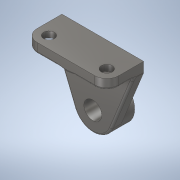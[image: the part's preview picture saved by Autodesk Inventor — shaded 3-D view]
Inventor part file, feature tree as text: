
AUTODESK INVENTOR PART (.ipt)
format: ipt  version: 2020 (Build 240168000, 168)  size: 650,240 bytes
history: native  units: mm
features: extrude x5, sketch x4, fillet x2, plane x1, rib x1
ambient origin geometry x8: Origin, YZ Plane, XZ Plane, XY Plane, X Axis, Y Axis, Z Axis, Center Point
bodies: Solid1 (feature_tree)
feature tree (13):
  extrude  "Extrusion1"  Depth=41.0mm
  sketch  "Sketch2"  dims[d2=18.0mm d3=22.0mm d4=0.0mm]
  extrude  "Extrusion2"  Depth=22.0mm TaperAngle=0.0deg
  extrude  "Extrusion3"  Depth=41.0mm
  plane  "Work Plane1"
  rib  "Rib1"
  sketch  "Sketch6"  dims[d7=10.0mm d8=10.0mm d9=0.0mm d10=27.0mm d11=0.0mm d12=-41.0mm d17=1.0mm d18=10.0mm d19=0.0mm d20=0.0mm d21=1.0mm d22=1.0mm d23=11.0mm d24=22.0mm d25=22.0mm d26=11.0mm d27=12.0mm d28=12.0mm d29=12.0mm d30=12.0mm d31=27.0mm d32=0.0mm d33=4.0mm d34=0.0mm d35=12.0mm d37=2.0mm]
  extrude  "Extrusion4"  Depth=10.0mm TaperAngle=0.0deg
  extrude  "Extrusion5"  Depth=27.0mm TaperAngle=0.0deg
  fillet  "Fillet1"  [1 undecoded]
  fillet  "Fillet3"  Radius=1.0mm
  sketch  "Sketch1"  dims[d0=40.0mm d1=41.0mm]
  sketch  "Sketch5"  dims[d5=82.0mm d6=41.0mm]
note: 1 required parameter value undecoded (feature->parameter linkage not recoverable at this tier; creation-order binding heuristic only, values carry confidence <= 0.55)
